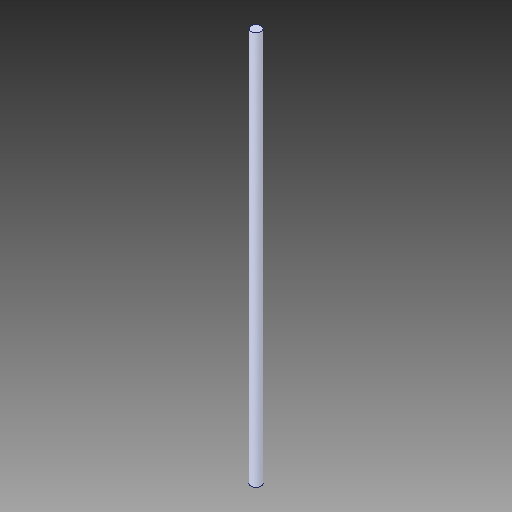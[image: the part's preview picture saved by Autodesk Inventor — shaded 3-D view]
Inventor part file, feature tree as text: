
AUTODESK INVENTOR PART (.ipt)
format: ipt  version: 2018 (Build 220112000, 112)  size: 102,400 bytes
history: native  units: in
note: dims shown in document units (in); Inventor stores cm internally (conversion verified against a paired STEP export)
features: extrude x1, sketch x1
ambient origin geometry x8: Origin, YZ Plane, XZ Plane, XY Plane, X Axis, Y Axis, Z Axis, Center Point
bodies: Body1 (feature_tree)
feature tree (2):
  extrude  "Extrusion1"  Depth=9.8425in TaperAngle=0.0deg
  sketch  "Sketch1"  dims[d0=0.25in d1=9.8425in d2=0.0in]
